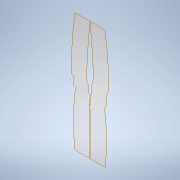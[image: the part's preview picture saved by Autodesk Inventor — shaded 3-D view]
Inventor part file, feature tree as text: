
AUTODESK INVENTOR PART (.ipt)
format: ipt  version: 2022 (Build 260153000, 153)  size: 2,853,376 bytes
history: native  units: mm
features: sketch x7, sweep x2, extrude x1, boolean_combine x1, other x1, surface_op x1
ambient origin geometry x8: Origin, YZ Plane, XZ Plane, XY Plane, X Axis, Y Axis, Z Axis, Center Point
bodies: Solid4 (feature_tree), Solid5 (feature_tree)
feature tree (13):
  sketch  "Sketch1"  dims[d14=330.0mm d15=0.0mm d16=0.0mm]
  sketch  "Sketch2"  dims[d17=330.0mm d18=90.0deg]
  sketch  "3D Sketch1"
  sketch  "3D Sketch2"
  sweep  "Sweep4"
  sweep  "Sweep5"
  extrude  "Extrusion1"  Depth=30.0mm
  boolean_combine  "Combine1"
  sketch  "Sketch4"  dims[d19=0.0mm d20=0.0mm d21=30.0mm]
  sketch  "Sketch5"  dims[d22=670.0mm d23=36.0mm d24=0.0mm d25=0.0mm]
  sketch  "3D Sketch3"
  other  "Srf1"
  surface_op  "Boundary Patch1"
